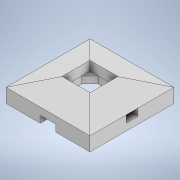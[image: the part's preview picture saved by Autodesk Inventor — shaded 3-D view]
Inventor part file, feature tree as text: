
AUTODESK INVENTOR PART (.ipt)
format: ipt  version: 2020 (Build 240168000, 168)  size: 205,824 bytes
history: native  units: mm
features: extrude x9, sketch x9
ambient origin geometry x8: Origin, YZ Plane, XZ Plane, XY Plane, X Axis, Y Axis, Z Axis, Center Point
bodies: Solid1 (feature_tree)
feature tree (18):
  extrude  "Extrusion1"  Depth=10.0mm
  extrude  "Extrusion2"  Depth=5.0mm
  extrude  "Extrusion3"  Depth=12.0mm
  extrude  "Extrusion4"  Depth=1.0mm
  extrude  "Extrusion5"  Depth=2.0mm TaperAngle=0.0deg
  extrude  "Extrusion6"  Depth=4.0mm
  extrude  "Extrusion7"  Depth=2.0mm
  extrude  "Extrusion8"  Depth=1.0mm TaperAngle=0.0deg
  extrude  "Extrusion9"  Depth=4.0mm
  sketch  "Sketch1"  dims[d0=10.0mm d1=10.0mm]
  sketch  "Sketch2"  dims[d2=5.0mm d3=5.0mm]
  sketch  "Sketch3"  dims[d4=12.0mm d5=12.0mm]
  sketch  "Sketch4"  dims[d6=1.0mm d7=1.0mm]
  sketch  "Sketch5"  dims[d8=2.0mm d9=0.0mm d10=11.5mm d11=0.0mm]
  sketch  "Sketch6"  dims[d13=4.0mm d14=4.0mm]
  sketch  "Sketch7"  dims[d15=2.0mm d16=2.0mm]
  sketch  "Sketch8"  dims[d17=23.25mm d18=0.0mm d19=1.0mm d20=0.0mm]
  sketch  "Sketch9"  dims[d21=25.0mm d22=0.0mm d23=4.0mm d24=23.25mm d25=0.0mm d26=41.75mm d27=0.0mm d28=11.625mm d29=0.0mm d30=4.0mm d31=4.0mm d32=105.0mm d33=0.0mm d34=1.1mm d35=1.1mm d36=2.75mm d37=0.0mm]
